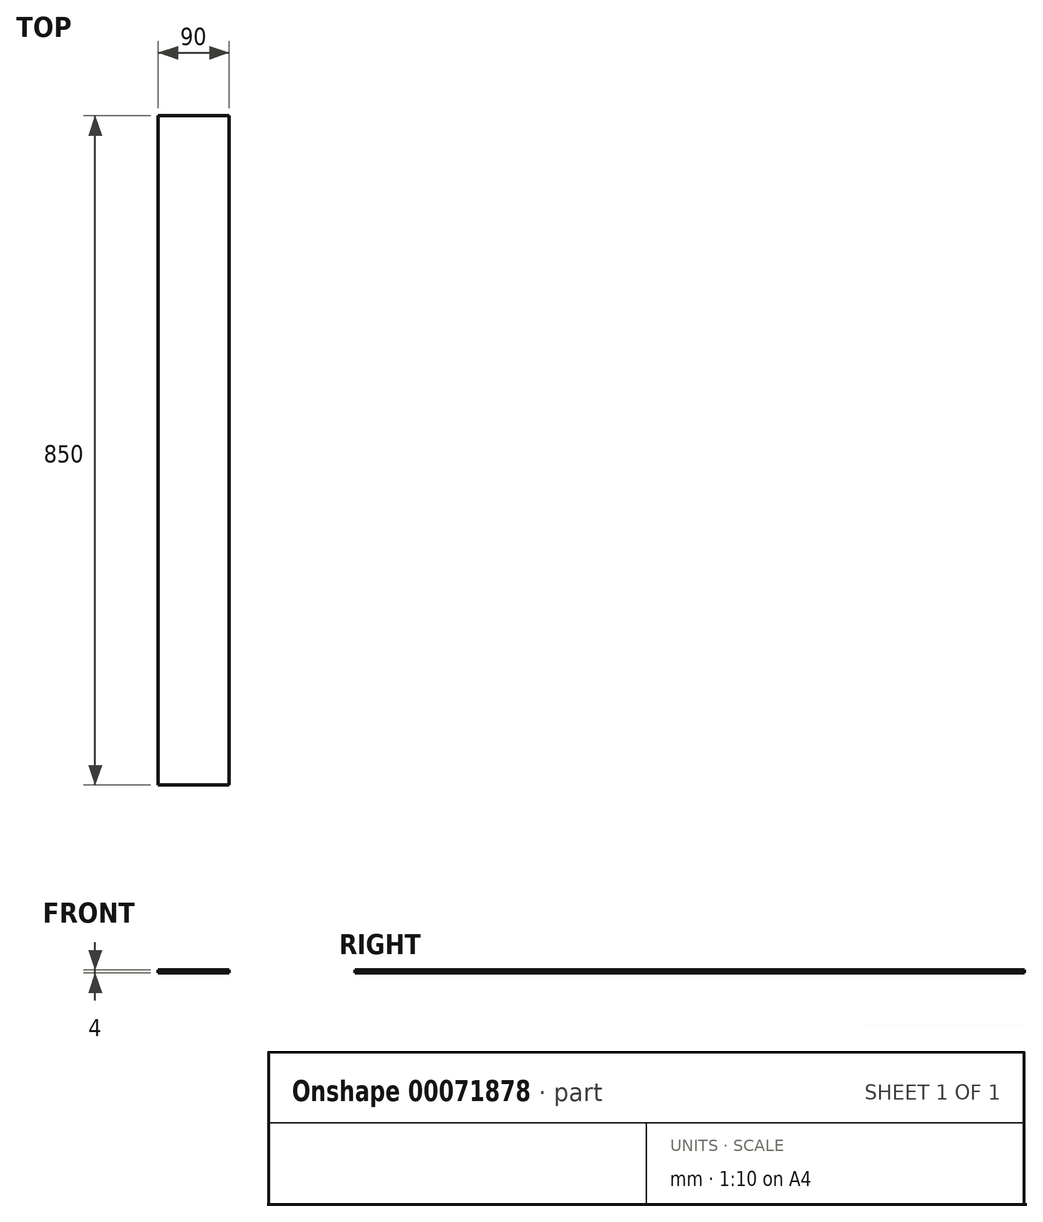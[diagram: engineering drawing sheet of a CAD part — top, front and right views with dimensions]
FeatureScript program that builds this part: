
annotation { "Feature Type Name" : "Feature", "Feature Type Description" : "" }
export const myFeature = defineFeature(function(context is Context, id is Id, definition is map)
    precondition{}
    {
        {
            var Q0;
            Q0=qCreatedBy(makeId("Top.planeOp"),FACE);
            var sketch = newSketch(context, id + "F0", { "sketchPlane" : qUnion([Q0])});
            skLineSegment(sketch, "E0.bottom", {"start": v(-45, -425) * mm, "end": v(45, -425) * mm});
            skLineSegment(sketch, "E0.top", {"start": v(-45, 425) * mm, "end": v(45, 425) * mm});
            skLineSegment(sketch, "E0.left", {"start": v(-45, -425) * mm, "end": v(-45, 425) * mm});
            skLineSegment(sketch, "E0.right", {"start": v(45, -425) * mm, "end": v(45, 425) * mm});
            skPoint(sketch, "E0.middle", {"position": v(0, 0) * mm});
            skSolve(sketch);
        }
        {
            var Q0;
            Q0 = qSketchRegion(id + "F0", true);
            extrude(context, id + "F1", {"entities" : qUnion([Q0]), "depth" : 4 * mm});
        }
    });
